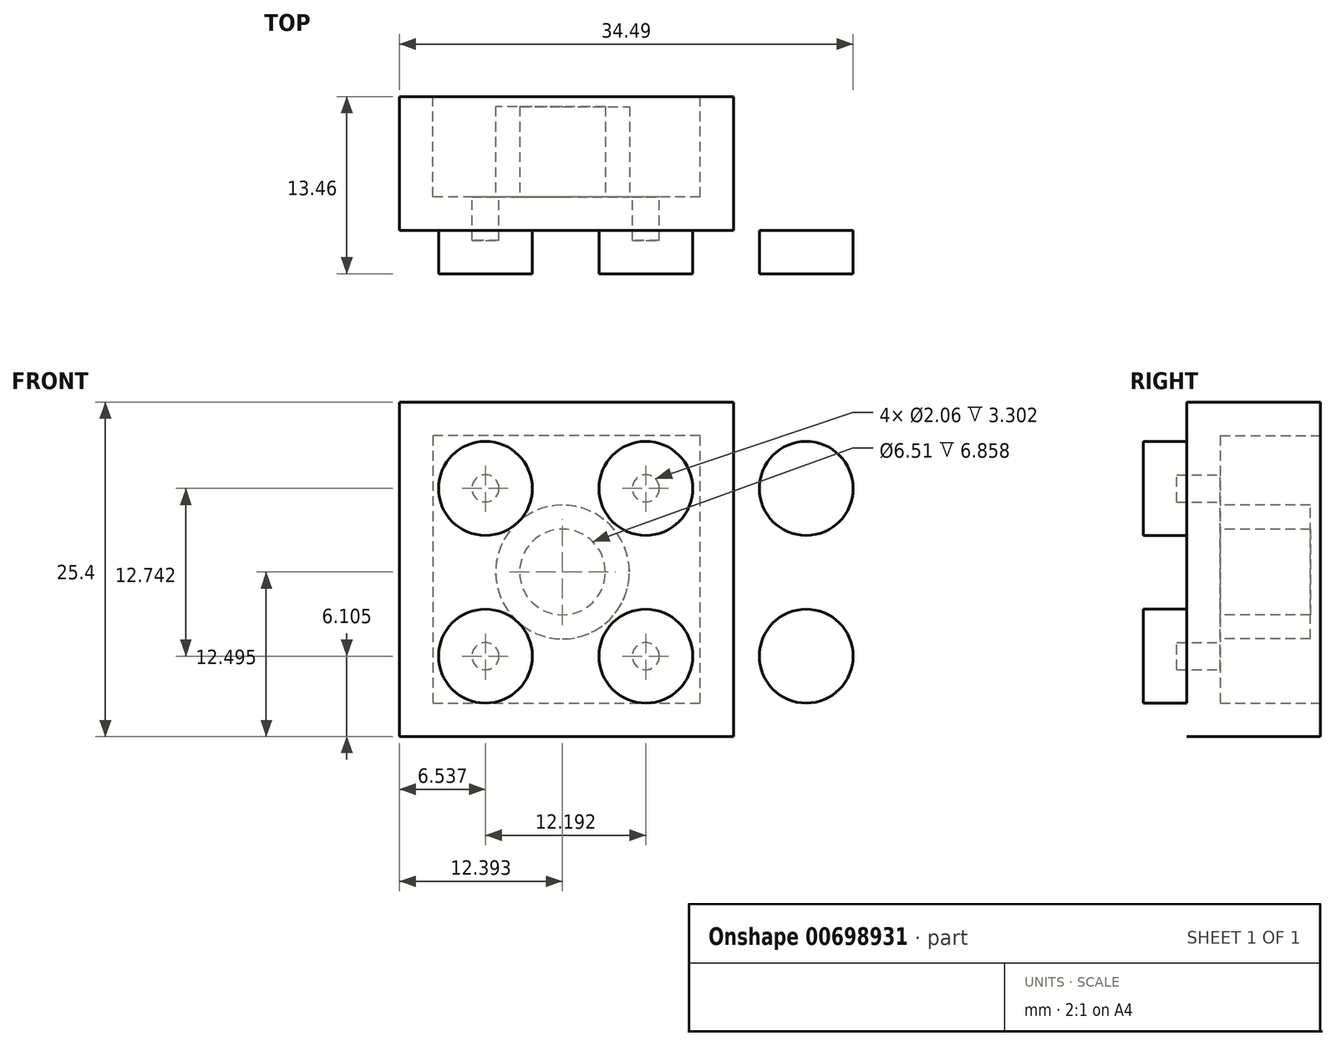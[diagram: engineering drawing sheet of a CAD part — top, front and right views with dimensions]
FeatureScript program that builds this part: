
annotation { "Feature Type Name" : "Feature", "Feature Type Description" : "" }
export const myFeature = defineFeature(function(context is Context, id is Id, definition is map)
    precondition{}
    {
        {
            var Q0;
            Q0=qCreatedBy(makeId("Front.planeOp"),FACE);
            var sketch = newSketch(context, id + "F0", { "sketchPlane" : qUnion([Q0])});
            skLineSegment(sketch, "E0", {"start": v(-48.61, 28.2) * mm, "end": v(-48.61, 2.8) * mm});
            skLineSegment(sketch, "E1", {"start": v(-48.61, 2.8) * mm, "end": v(-23.21, 2.8) * mm});
            skLineSegment(sketch, "E2", {"start": v(-23.21, 2.8) * mm, "end": v(-23.21, 28.2) * mm});
            skLineSegment(sketch, "E3", {"start": v(-23.21, 28.2) * mm, "end": v(-48.61, 28.2) * mm});
            skSolve(sketch);
        }
        {
            var Q0;
            Q0 = qSketchRegion(id + "F0", true);
            extrude(context, id + "F1", {"entities" : qUnion([Q0]), "depth" : 10.16 * mm, "offsetDistance" : 25.4 * mm});
        }
        {
            var Q0;
            Q0=makeQuery(id+"F1.opExtrude","CAP_FACE",FACE,{"disambiguationData":[OSD([sQuery(id+"F0.wireOp",EDGE,"E0"),sQuery(id+"F0.wireOp",EDGE,"E1"),sQuery(id+"F0.wireOp",EDGE,"E2"),sQuery(id+"F0.wireOp",EDGE,"E3")])],"isStart":false});
            var sketch = newSketch(context, id + "F2", { "sketchPlane" : qUnion([Q0])});
            skCircle(sketch, "E4", {"center": v(-42.07, 21.66) * mm, "radius": 3.57 * mm});
            skCircle(sketch, "E5", {"center": v(-42.07, 8.92) * mm, "radius": 3.57 * mm});
            skCircle(sketch, "E6.1.0.0", {"center": v(-29.88, 21.66) * mm, "radius": 3.57 * mm});
            skCircle(sketch, "E6.1.0.1", {"center": v(-29.88, 8.92) * mm, "radius": 3.57 * mm});
            skCircle(sketch, "E6.2.0.0", {"center": v(-17.69, 21.66) * mm, "radius": 3.57 * mm});
            skCircle(sketch, "E6.2.0.1", {"center": v(-17.69, 8.92) * mm, "radius": 3.57 * mm});
            skLineSegment(sketch, "E6.direction1", {"start": v(-42.07, 8.92) * mm, "end": v(-29.88, 8.92) * mm, "construction": true});
            skSolve(sketch);
        }
        {
            var Q0;
            Q0 = qSketchRegion(id + "F2", true);
            extrude(context, id + "F3", {"entities" : qUnion([Q0]), "operationType" : NewBodyOperationType.ADD, "depth" : 3.3 * mm, "offsetDistance" : 25.4 * mm});
        }
        {
            var Q0;
            Q0=makeQuery(id+"F1.opExtrude","CAP_FACE",FACE,{"disambiguationData":[OSD([sQuery(id+"F0.wireOp",EDGE,"E0"),sQuery(id+"F0.wireOp",EDGE,"E1"),sQuery(id+"F0.wireOp",EDGE,"E2"),sQuery(id+"F0.wireOp",EDGE,"E3")])],"isStart":true});
            shell(context, id + "F4", {"entities" : qUnion([Q0]), "thickness" : 2.54 * mm});
        }
        {
            var Q0;
            Q0=makeQuery(id+"F4.opShell","OFFSET_FACE",FACE,{"disambiguationData":[OSD([sQuery(id+"F0.wireOp",EDGE,"E0"),sQuery(id+"F0.wireOp",EDGE,"E1"),sQuery(id+"F0.wireOp",EDGE,"E2"),sQuery(id+"F0.wireOp",EDGE,"E3")])]});
            var sketch = newSketch(context, id + "F5", { "sketchPlane" : qUnion([Q0])});
            skCircle(sketch, "E7", {"center": v(36.22, 15.3) * mm, "radius": 5.08 * mm});
            skCircle(sketch, "E8", {"center": v(36.22, 15.3) * mm, "radius": 3.25 * mm});
            skSolve(sketch);
        }
        {
            var Q0;
            Q0 = qSketchRegion(id + "F5", true);
            extrude(context, id + "F6", {"entities" : qUnion([Q0]), "operationType" : NewBodyOperationType.ADD, "depth" : 6.86 * mm, "offsetDistance" : 25.4 * mm});
        }
    });
